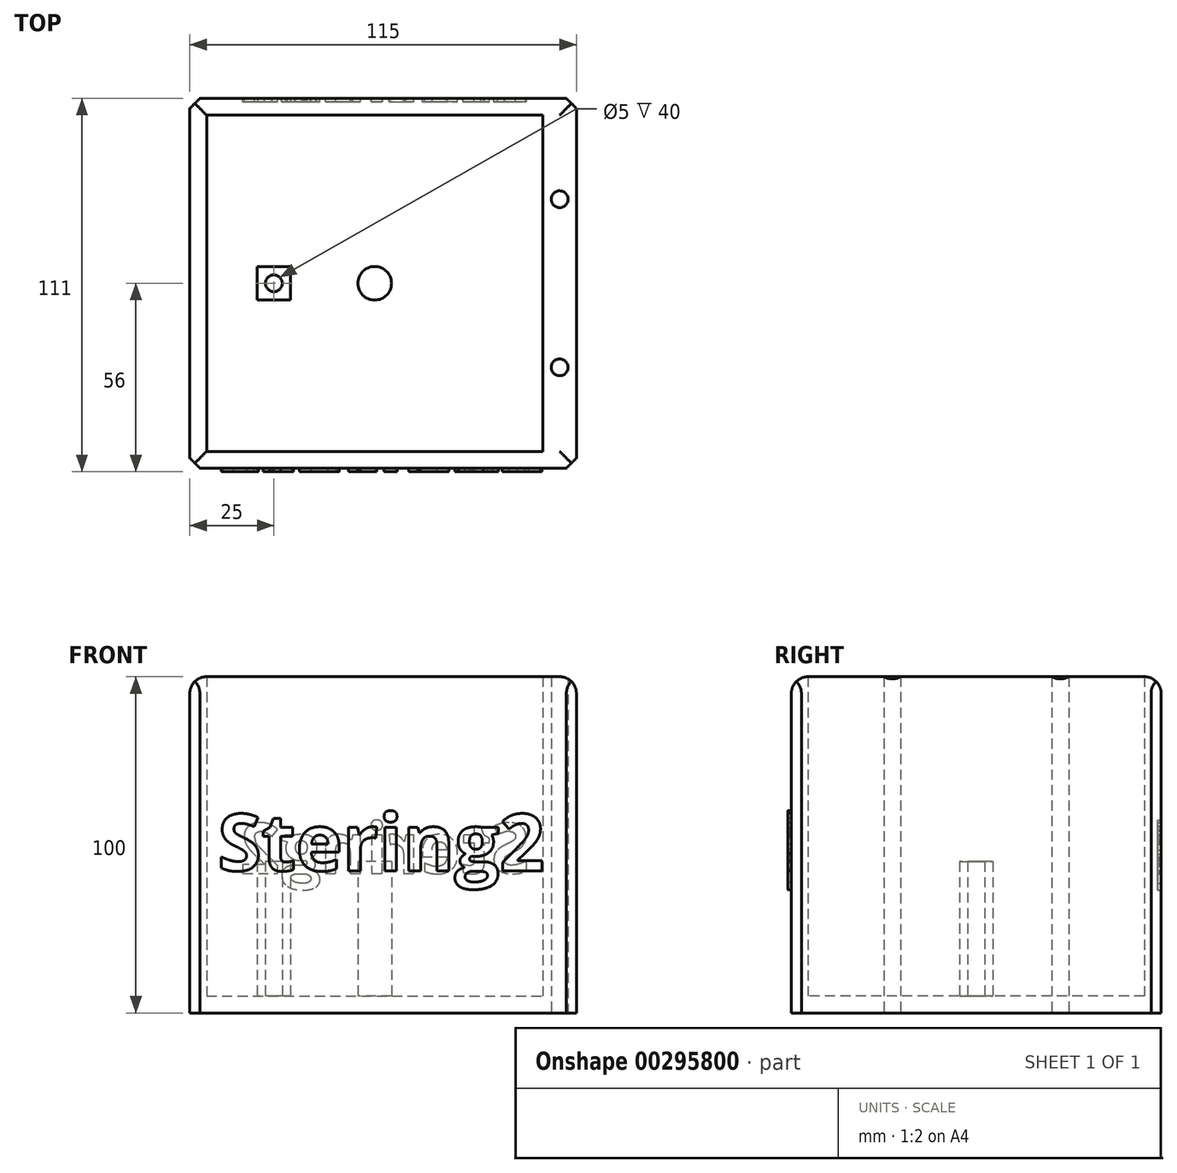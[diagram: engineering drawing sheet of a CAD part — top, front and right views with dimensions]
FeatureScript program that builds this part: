
annotation { "Feature Type Name" : "Feature", "Feature Type Description" : "" }
export const myFeature = defineFeature(function(context is Context, id is Id, definition is map)
    precondition{}
    {
        {
            var Q0;
            Q0=qCreatedBy(makeId("Top.planeOp"),FACE);
            var sketch = newSketch(context, id + "F0", { "sketchPlane" : qUnion([Q0])});
            skLineSegment(sketch, "E0.bottom", {"start": v(-50, 50) * mm, "end": v(50, 50) * mm});
            skLineSegment(sketch, "E0.top", {"start": v(-50, -50) * mm, "end": v(50, -50) * mm});
            skLineSegment(sketch, "E0.left", {"start": v(-50, 50) * mm, "end": v(-50, -50) * mm});
            skLineSegment(sketch, "E0.right", {"start": v(50, 50) * mm, "end": v(50, -50) * mm});
            skPoint(sketch, "E0.middle", {"position": v(0, 0) * mm});
            skLineSegment(sketch, "E1.bottom", {"start": v(-55, 55) * mm, "end": v(55, 55) * mm});
            skLineSegment(sketch, "E1.top", {"start": v(-55, -55) * mm, "end": v(55, -55) * mm});
            skLineSegment(sketch, "E1.left", {"start": v(-55, 55) * mm, "end": v(-55, -55) * mm});
            skLineSegment(sketch, "E1.right", {"start": v(55, 55) * mm, "end": v(55, -55) * mm});
            skLineSegment(sketch, "E2.bottom", {"start": v(55, 55) * mm, "end": v(55, 55) * mm});
            skLineSegment(sketch, "E2.top", {"start": v(55, -55) * mm, "end": v(55, -55) * mm});
            skLineSegment(sketch, "E3.bottom", {"start": v(55, 55) * mm, "end": v(60, 55) * mm});
            skLineSegment(sketch, "E3.top", {"start": v(55, -55) * mm, "end": v(60, -55) * mm});
            skLineSegment(sketch, "E3.right", {"start": v(60, 55) * mm, "end": v(60, -55) * mm});
            skSolve(sketch);
        }
        {
            var Q0;
            Q0 = qSketchRegion(id + "F0", true);
            extrude(context, id + "F1", {"entities" : qUnion([Q0]), "depth" : 100 * mm});
        }
        {
            var Q0;
            Q0=qCreatedBy(makeId("Front.planeOp"),FACE);
            var sketch = newSketch(context, id + "F2", { "sketchPlane" : qUnion([Q0])});
            skLineSegment(sketch, "E4.bottom", {"start": v(-55, 0) * mm, "end": v(60, 0) * mm});
            skLineSegment(sketch, "E4.top", {"start": v(-55, 5) * mm, "end": v(60, 5) * mm});
            skLineSegment(sketch, "E4.left", {"start": v(-55, 0) * mm, "end": v(-55, 5) * mm});
            skLineSegment(sketch, "E4.right", {"start": v(60, 0) * mm, "end": v(60, 5) * mm});
            skSolve(sketch);
        }
        {
            var Q0;
            Q0 = qSketchRegion(id + "F2", true);
            extrude(context, id + "F3", {"entities" : qUnion([Q0]), "operationType" : NewBodyOperationType.ADD, "endBound" : BoundingType.SYMMETRIC, "depth" : 105 * mm});
        }
        {
            var Q0;
            Q0=makeQuery(id+"F3.opExtrude","SWEPT_FACE",FACE,{"disambiguationData":[OSD([sQuery(id+"F2.wireOp",EDGE,"E4.top")])]});
            var sketch = newSketch(context, id + "F4", { "sketchPlane" : qUnion([Q0])});
            skLineSegment(sketch, "E5", {"start": v(55, 55) * mm, "end": v(55, -55) * mm, "construction": true});
            skLineSegment(sketch, "E6", {"start": v(60, 25) * mm, "end": v(-55, 25) * mm, "construction": true});
            skLineSegment(sketch, "E7", {"start": v(60, -25) * mm, "end": v(-55, -25) * mm, "construction": true});
            skCircle(sketch, "E8", {"center": v(55, 25) * mm, "radius": 2.5 * mm});
            skCircle(sketch, "E9", {"center": v(55, -25) * mm, "radius": 2.5 * mm});
            skSolve(sketch);
        }
        {
            var Q0;
            Q0 = qSketchRegion(id + "F4", true);
            var Q1;
            Q1 = qSketchRegion(id + "FO1JOWXqG4Ol2i1_1", true);
            extrude(context, id + "F5", {"entities" : qUnion([Q0, Q1]), "operationType" : NewBodyOperationType.REMOVE, "endBound" : BoundingType.UP_TO_NEXT, "depth" : 25 * mm, "hasSecondDirection" : true, "secondDirectionBound" : SecondDirectionBoundingType.THROUGH_ALL, "secondDirectionOppositeDirection" : true, "secondDirectionDepth" : 25 * mm});
        }
        {
            var Q0;
            Q0=makeQuery(id+"F1.opExtrude","SWEPT_FACE",FACE,{"disambiguationData":[OSD([sQuery(id+"F0.wireOp",EDGE,"E1.top"),sQuery(id+"F0.wireOp",EDGE,"E3.top")])]});
            var sketch = newSketch(context, id + "F6", { "sketchPlane" : qUnion([Q0])});
            skText(sketch, "E10", { "text": "Stering2", "fontName": "OpenSans-Bold.ttf"});
            const initialGuessF6  = {"E10": [-0.04665, 0.0423, 1, 0, 0.01695]};
            skSetInitialGuess(sketch, initialGuessF6);
            skSolve(sketch);
        }
        {
            var Q0;
            Q0 = qSketchRegion(id + "F6", true);
            var Q1;
            Q1=makeQuery(id+"F1.opExtrude","SWEPT_FACE",FACE,{"disambiguationData":[OSD([sQuery(id+"F0.wireOp",EDGE,"E1.bottom"),sQuery(id+"F0.wireOp",EDGE,"E3.bottom")])]});
            extrude(context, id + "F7", {"entities" : qUnion([Q0, Q1]), "operationType" : NewBodyOperationType.ADD, "depth" : 1 * mm});
        }
        {
            var Q0;
            Q0=makeQuery(id+"F1.opExtrude","SWEPT_FACE",FACE,{"disambiguationData":[OSD([sQuery(id+"F0.wireOp",EDGE,"E1.bottom"),sQuery(id+"F0.wireOp",EDGE,"E3.bottom")])]});
            var sketch = newSketch(context, id + "F8", { "sketchPlane" : qUnion([Q0])});
            skText(sketch, "E11", { "text": "Stering2", "fontName": "OpenSans-Bold.ttf"});
            const initialGuessF8  = {"E11": [-0.0461, 0.04154, 1, 0, 0.015]};
            skSetInitialGuess(sketch, initialGuessF8);
            skSolve(sketch);
        }
        {
            var Q0;
            Q0 = qSketchRegion(id + "F8", true);
            extrude(context, id + "F9", {"entities" : qUnion([Q0]), "operationType" : NewBodyOperationType.REMOVE, "oppositeDirection" : true, "depth" : 1 * mm});
        }
        {
            var Q0;
            Q0=makeQuery(id+"F3.opExtrude","SWEPT_FACE",FACE,{"disambiguationData":[OSD([sQuery(id+"F2.wireOp",EDGE,"E4.top")])]});
            var sketch = newSketch(context, id + "F10", { "sketchPlane" : qUnion([Q0])});
            skCircle(sketch, "E12", {"center": v(0, 0) * mm, "radius": 5 * mm});
            skLineSegment(sketch, "E13.bottom", {"start": v(-25, -5) * mm, "end": v(-35, -5) * mm});
            skLineSegment(sketch, "E13.top", {"start": v(-25, 5) * mm, "end": v(-35, 5) * mm});
            skLineSegment(sketch, "E13.left", {"start": v(-25, -5) * mm, "end": v(-25, 5) * mm});
            skLineSegment(sketch, "E13.right", {"start": v(-35, -5) * mm, "end": v(-35, 5) * mm});
            skPoint(sketch, "E13.middle", {"position": v(-30, 0) * mm});
            skCircle(sketch, "E14", {"center": v(-30, 0) * mm, "radius": 2.5 * mm});
            skSolve(sketch);
        }
        {
            var Q0;
            Q0=makeQuery(id+"F10.imprint","IMPRINT",FACE,{"disambiguationData":[TD([[makeQuery(id+"F10.imprint","IMPRINT",EDGE,{"derivedFrom":sQuery(id+"F10.wireOp",EDGE,"E12")}),1.0]])]});
            var Q1;
            Q1=makeQuery(id+"F10.imprint","IMPRINT",FACE,{"disambiguationData":[TD([[makeQuery(id+"F10.imprint","IMPRINT",EDGE,{"derivedFrom":sQuery(id+"F10.wireOp",EDGE,"E13.bottom")}),-1.0]])]});
            extrude(context, id + "F11", {"entities" : qUnion([Q0, Q1]), "operationType" : NewBodyOperationType.ADD, "depth" : 40 * mm});
        }
        {
            var Q0;
            Q0=makeQuery(id+"F1.opExtrude","SWEPT_EDGE",EDGE,{"disambiguationData":[OSD([sQuery(id+"F0.wireOp",EDGE,"E3.top"),sQuery(id+"F0.wireOp",EDGE,"E3.right")])]});
            var Q1;
            Q1=makeQuery(id+"F1.opExtrude","SWEPT_EDGE",EDGE,{"disambiguationData":[OSD([sQuery(id+"F0.wireOp",EDGE,"E1.top"),sQuery(id+"F0.wireOp",EDGE,"E1.left")])]});
            var Q2;
            Q2=makeQuery(id+"F1.opExtrude","SWEPT_EDGE",EDGE,{"disambiguationData":[OSD([sQuery(id+"F0.wireOp",EDGE,"E3.bottom"),sQuery(id+"F0.wireOp",EDGE,"E3.right")])]});
            var Q3;
            Q3=makeQuery(id+"F1.opExtrude","SWEPT_EDGE",EDGE,{"disambiguationData":[OSD([sQuery(id+"F0.wireOp",EDGE,"E1.bottom"),sQuery(id+"F0.wireOp",EDGE,"E1.left")])]});
            chamfer(context, id + "F12", {"entities" : qUnion([Q0, Q1, Q2, Q3]), "width" : 3 * mm, "tangentPropagation" : true});
        }
        {
            var Q0;
            Q0=makeQuery(id+"F1.opExtrude","CAP_EDGE",EDGE,{"disambiguationData":[OSD([sQuery(id+"F0.wireOp",EDGE,"E3.right")])],"isStart":false});
            var Q1;
            Q1=makeQuery(id+"F1.opExtrude","CAP_EDGE",EDGE,{"disambiguationData":[OSD([sQuery(id+"F0.wireOp",EDGE,"E1.bottom"),sQuery(id+"F0.wireOp",EDGE,"E3.bottom")])],"isStart":false});
            var Q2;
            Q2=makeQuery(id+"F1.opExtrude","CAP_EDGE",EDGE,{"disambiguationData":[OSD([sQuery(id+"F0.wireOp",EDGE,"E1.left")])],"isStart":false});
            var Q3;
            Q3=makeQuery(id+"F1.opExtrude","CAP_EDGE",EDGE,{"disambiguationData":[OSD([sQuery(id+"F0.wireOp",EDGE,"E1.top"),sQuery(id+"F0.wireOp",EDGE,"E3.top")])],"isStart":false});
            fillet(context, id + "F13", {"entities" : qUnion([Q0, Q1, Q2, Q3]), "radius" : 5 * mm, "tangentPropagation" : true, "allowEdgeOverflow" : false});
        }
    });
